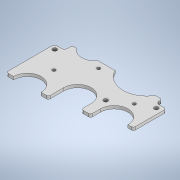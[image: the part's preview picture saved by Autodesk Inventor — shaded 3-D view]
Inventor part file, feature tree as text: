
AUTODESK INVENTOR PART (.ipt)
format: ipt  version: 2021 (Build 250183000, 183)  size: 257,536 bytes
history: native  units: mm
features: sketch x5, extrude x4, hole x2, fillet x2, projected_geometry x1
ambient origin geometry x8: Origin, YZ Plane, XZ Plane, XY Plane, X Axis, Y Axis, Z Axis, Center Point
bodies: Solid1 (feature_tree)
feature tree (14):
  extrude  "Extrusion1"  Depth=112.5mm
  extrude  "Extrusion2"  Depth=3.0mm
  sketch  "Sketch3"  dims[d5=27.7mm d6=27.7mm]
  hole  "Hole1"  [1 undecoded]
  extrude  "Extrusion3"  Depth=27.7mm
  extrude  "Extrusion4"  Depth=112.5mm
  fillet  "Fillet1"  Radius=37.0mm
  hole  "Hole2"  [1 undecoded]
  fillet  "Fillet2"  Radius=30.9mm
  sketch  "Sketch1"  dims[d0=112.5mm d1=116.5mm]
  sketch  "Sketch2"  dims[d2=3.0mm d3=0.0mm d4=47.7mm]
  projected_geometry  "Projected Loop1"
  sketch  "Sketch4"  dims[d7=27.7mm d8=27.7mm]
  sketch  "Sketch5"  dims[d9=116.5mm d10=112.5mm d13=37.0mm d14=18.5mm d15=30.9mm d16=5.0mm d17=0.0mm d18=19.5mm d19=35.0mm d20=35.0mm d21=4.7mm d22=5.5mm d23=13.25mm d24=30.0mm d25=50.0mm d26=5.4mm d27=5.4mm d29=18.5mm d31=10.0mm d32=2.0mm d33=4.2mm d34=6.0mm d35=4.0mm d36=2.0mm d37=90.0deg d38=8.0mm d39=20.594885mm d40=10.0mm d41=0.0mm d42=6.0mm d43=6.0mm d44=6.0mm d45=14.0mm d46=40.0mm d47=4.2mm d48=14.0mm d49=4.2mm d50=4.2mm d52=3.0mm d53=10.0mm d54=0.0mm d55=27.7mm d56=47.7mm d57=25.8mm d58=28.0mm d59=23.25mm d60=2.0mm d61=27.7mm d62=23.25mm d63=37.0mm d64=17.5mm d65=17.5mm d66=16.0mm d67=2.0mm d68=13.0mm d69=34.0mm d70=36.0mm d71=2.0mm d72=11.0mm d73=13.0mm d74=3.2mm d75=6.0mm d76=4.0mm d77=2.0mm d78=90.0deg d79=8.0mm d80=20.594885mm d81=2.0mm]
note: 2 required parameter values undecoded (feature->parameter linkage not recoverable at this tier; creation-order binding heuristic only, values carry confidence <= 0.55)
